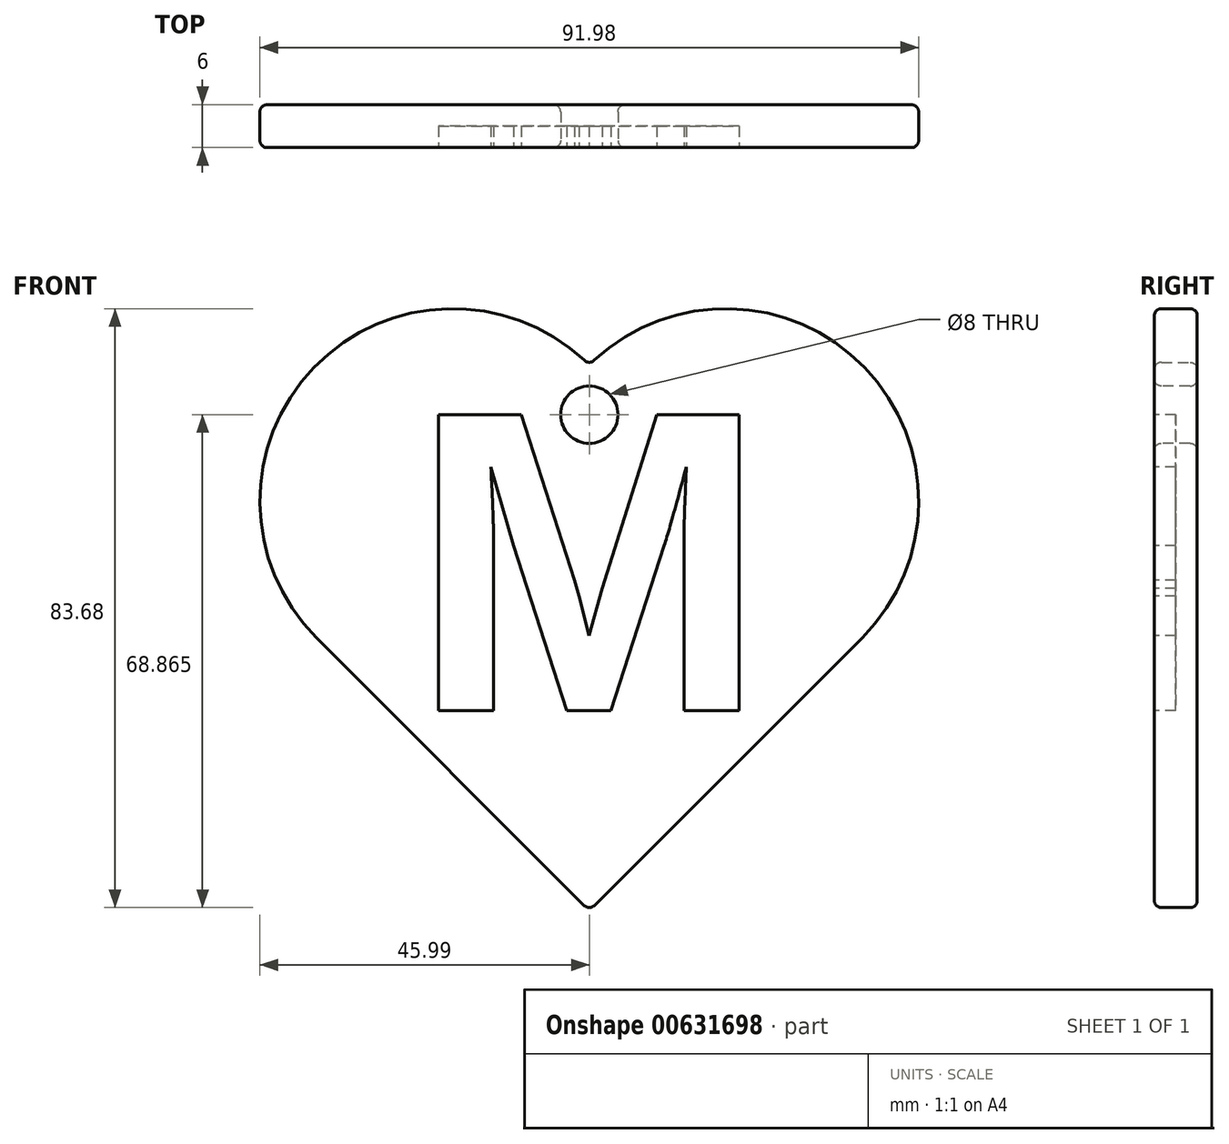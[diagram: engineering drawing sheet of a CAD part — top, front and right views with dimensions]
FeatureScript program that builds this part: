
annotation { "Feature Type Name" : "Feature", "Feature Type Description" : "" }
export const myFeature = defineFeature(function(context is Context, id is Id, definition is map)
    precondition{}
    {
        {
            var Q0;
            Q0=qCreatedBy(makeId("Front.planeOp"),FACE);
            var sketch = newSketch(context, id + "F0", { "sketchPlane" : qUnion([Q0])});
            skLineSegment(sketch, "E0.bottom", {"start": v(0, -38.1) * mm, "end": v(-38.1, 0) * mm});
            skLineSegment(sketch, "E0.top", {"start": v(38.1, 0) * mm, "end": v(0, 38.1) * mm});
            skLineSegment(sketch, "E0.left", {"start": v(0, -38.1) * mm, "end": v(38.1, 0) * mm});
            skLineSegment(sketch, "E0.right", {"start": v(-38.1, 0) * mm, "end": v(0, 38.1) * mm});
            skPoint(sketch, "E0.middle", {"position": v(0, 0) * mm});
            skLineSegment(sketch, "E1", {"start": v(0, 38.1) * mm, "end": v(0, -38.1) * mm, "construction": true});
            skCircle(sketch, "E2", {"center": v(-19.05, 19.05) * mm, "radius": 26.94 * mm});
            skCircle(sketch, "E3.MirrorC", {"center": v(19.05, 19.05) * mm, "radius": 26.94 * mm});
            skSolve(sketch);
        }
        {
            var Q0;
            Q0=qCreatedBy(makeId("Front.planeOp"),FACE);
            var sketch = newSketch(context, id + "F1", { "sketchPlane" : qUnion([Q0])});
            skText(sketch, "E4", { "text": "M", "fontName": "Arimo-Bold.ttf"});
            const initialGuessF1  = {"E4": [-0.0251, -0.01017, 1, 0, 0.04327]};
            skSetInitialGuess(sketch, initialGuessF1);
            skSolve(sketch);
        }
        {
            var Q0;
            {var subQ0=sQuery(id+"F0.wireOp",EDGE,"E0.top");Q0=makeQuery(id+"F0.imprint","IMPRINT",FACE,{"disambiguationData":[TD([[makeQuery(id+"F0.imprint","IMPRINT",EDGE,{"derivedFrom":subQ0}),-1.0]])]});}
            var Q1;
            {var subQ0=sQuery(id+"F0.wireOp",EDGE,"E0.top");Q1=makeQuery(id+"F0.imprint","IMPRINT",FACE,{"disambiguationData":[TD([[makeQuery(id+"F0.imprint","IMPRINT",EDGE,{"derivedFrom":subQ0}),1.0]])]});}
            var Q2;
            {var subQ0=sQuery(id+"F0.wireOp",EDGE,"E3.MirrorC");var subQ1=sQuery(id+"F0.wireOp",EDGE,"E2");var subQ3=makeQuery(id+"F0.imprint","INTERSECT",VERTEX,{"derivedFrom":[subQ1,subQ0]});Q2=makeQuery(id+"F0.imprint","IMPRINT",FACE,{"disambiguationData":[TD([[makeQuery(id+"F0.imprint","IMPRINT",EDGE,{"disambiguationData":[TD([[subQ3,-1.0]])],"derivedFrom":subQ1}),1.0]])]});}
            var Q3;
            {var subQ0=sQuery(id+"F0.wireOp",EDGE,"E0.right");Q3=makeQuery(id+"F0.imprint","IMPRINT",FACE,{"disambiguationData":[TD([[makeQuery(id+"F0.imprint","IMPRINT",EDGE,{"derivedFrom":subQ0}),-1.0]])]});}
            var Q4;
            {var subQ0=sQuery(id+"F0.wireOp",EDGE,"E0.right");Q4=makeQuery(id+"F0.imprint","IMPRINT",FACE,{"disambiguationData":[TD([[makeQuery(id+"F0.imprint","IMPRINT",EDGE,{"derivedFrom":subQ0}),1.0]])]});}
            var Q5;
            {var subQ0=sQuery(id+"F0.wireOp",EDGE,"E0.bottom");Q5=makeQuery(id+"F0.imprint","IMPRINT",FACE,{"disambiguationData":[TD([[makeQuery(id+"F0.imprint","IMPRINT",EDGE,{"derivedFrom":subQ0}),-1.0]])]});}
            extrude(context, id + "F2", {"entities" : qUnion([Q0, Q1, Q2, Q3, Q4, Q5]), "depth" : -6 * mm, "offsetDistance" : 25.4 * mm});
        }
        {
            var Q0;
            Q0 = qSketchRegion(id + "F1", true);
            extrude(context, id + "F3", {"entities" : qUnion([Q0]), "operationType" : NewBodyOperationType.REMOVE, "oppositeDirection" : true, "depth" : 3 * mm, "offsetDistance" : 25.4 * mm});
        }
        {
            var Q0;
            Q0=qCreatedBy(makeId("Front.planeOp"),FACE);
            var sketch = newSketch(context, id + "F4", { "sketchPlane" : qUnion([Q0])});
            skCircle(sketch, "E5", {"center": v(0, 31.18) * mm, "radius": 4 * mm});
            skLineSegment(sketch, "E6", {"start": v(55.78, 31.18) * mm, "end": v(-47.95, 31.18) * mm, "construction": true});
            skSolve(sketch);
        }
        {
            var Q0;
            Q0=makeQuery(id+"F4.imprint","IMPRINT",FACE,{"disambiguationData":[TD([[makeQuery(id+"F4.imprint","IMPRINT",EDGE,{"derivedFrom":sQuery(id+"F4.wireOp",EDGE,"E5")}),1.0]])]});
            extrude(context, id + "F5", {"entities" : qUnion([Q0]), "operationType" : NewBodyOperationType.REMOVE, "endBound" : BoundingType.UP_TO_NEXT, "oppositeDirection" : true, "depth" : 25.4 * mm, "offsetDistance" : 25.4 * mm});
        }
        {
            var Q0;
            Q0=makeQuery(id+"F2.opExtrude","SWEPT_FACE",FACE,{"disambiguationData":[OSD([sQuery(id+"F0.wireOp",EDGE,"E2")])]});
            var Q1;
            Q1=makeQuery(id+"F2.opExtrude","SWEPT_FACE",FACE,{"disambiguationData":[OSD([sQuery(id+"F0.wireOp",EDGE,"E3.MirrorC")])]});
            var Q2;
            Q2=makeQuery(id+"F2.opExtrude","SWEPT_FACE",FACE,{"disambiguationData":[OSD([sQuery(id+"F0.wireOp",EDGE,"E0.bottom")])]});
            var Q3;
            Q3=makeQuery(id+"F2.opExtrude","SWEPT_FACE",FACE,{"disambiguationData":[OSD([sQuery(id+"F0.wireOp",EDGE,"E0.left")])]});
            var Q4;
            Q4=makeQuery(id+"F5.boolean.opBoolean","COPY",FACE,{"derivedFrom":makeQuery(id+"F5.opExtrude","SWEPT_FACE",FACE,{"disambiguationData":[OSD([sQuery(id+"F4.wireOp",EDGE,"E5")])]})});
            fillet(context, id + "F6", {"entities" : qUnion([Q0, Q1, Q2, Q3, Q4]), "radius" : 1 * mm, "allowEdgeOverflow" : false});
        }
    });
